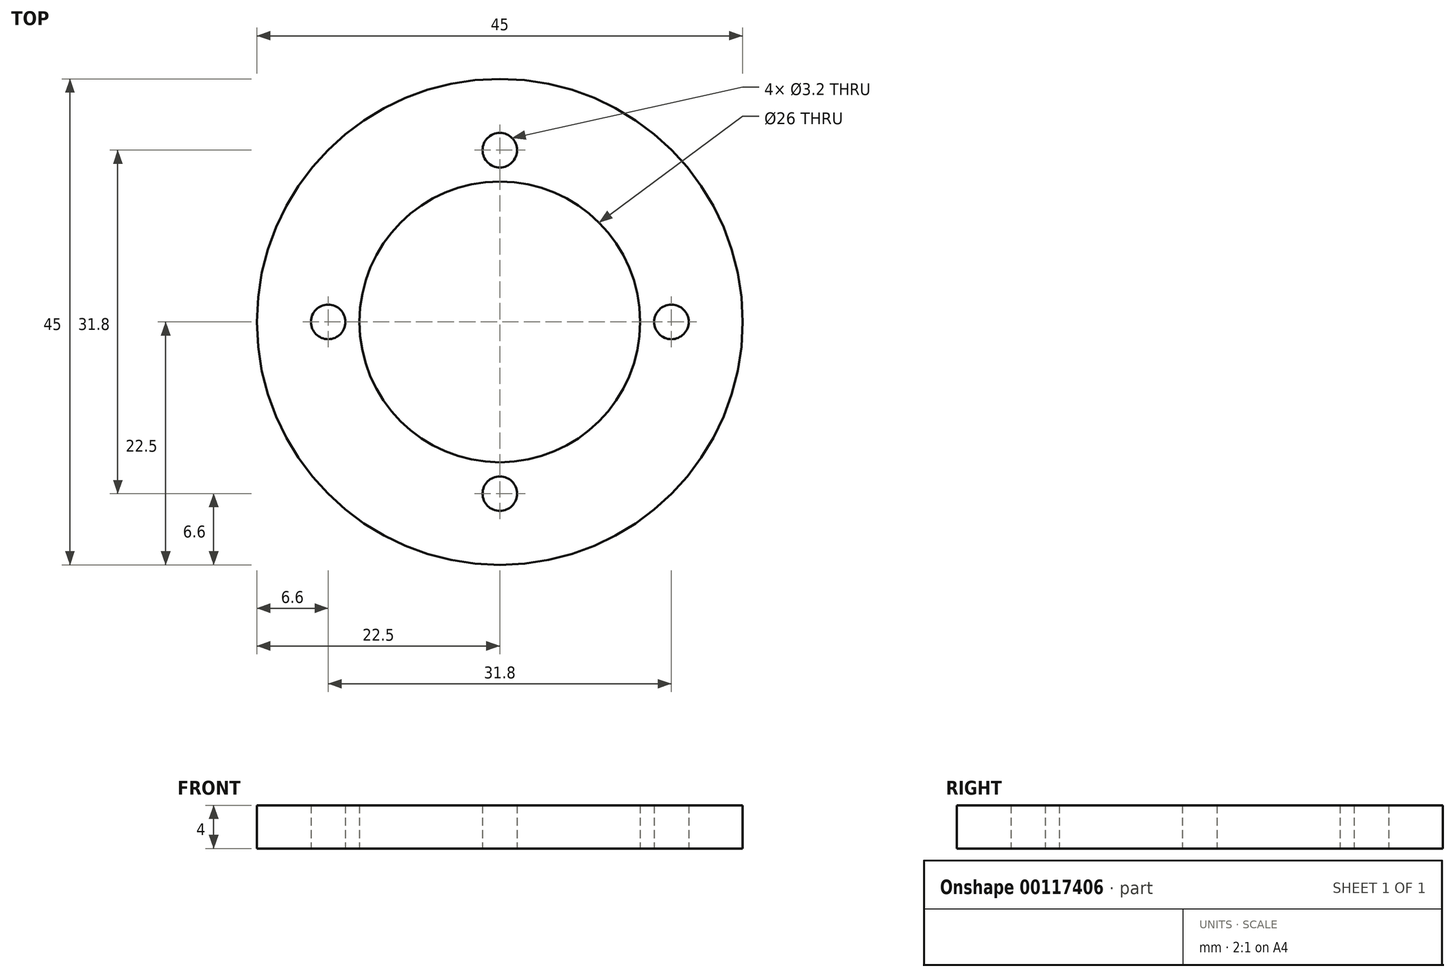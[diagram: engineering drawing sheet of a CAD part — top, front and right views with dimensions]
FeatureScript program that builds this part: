
annotation { "Feature Type Name" : "Feature", "Feature Type Description" : "" }
export const myFeature = defineFeature(function(context is Context, id is Id, definition is map)
    precondition{}
    {
        {
            var Q0;
            Q0=qCreatedBy(makeId("Top.planeOp"),FACE);
            var sketch = newSketch(context, id + "F0", { "sketchPlane" : qUnion([Q0])});
            skCircle(sketch, "E0", {"center": v(0, 0) * mm, "radius": 22.5 * mm});
            skCircle(sketch, "E1", {"center": v(0, 15.9) * mm, "radius": 1.6 * mm});
            skCircle(sketch, "E2.1.0", {"center": v(15.9, 0) * mm, "radius": 1.6 * mm});
            skCircle(sketch, "E2.2.0", {"center": v(0, -15.9) * mm, "radius": 1.6 * mm});
            skCircle(sketch, "E2.3.0", {"center": v(-15.9, 0) * mm, "radius": 1.6 * mm});
            skLineSegment(sketch, "E2.anchor1", {"start": v(0, 0) * mm, "end": v(0, 15.9) * mm, "construction": true});
            skLineSegment(sketch, "E2.anchor2", {"start": v(0, 0) * mm, "end": v(-15.9, 0) * mm, "construction": true});
            skLineSegment(sketch, "E3", {"start": v(-10.17, 17.5) * mm, "end": v(10.6, 17.5) * mm, "construction": true});
            skLineSegment(sketch, "E4", {"start": v(10.6, -17.5) * mm, "end": v(-12.33, -17.5) * mm, "construction": true});
            skCircle(sketch, "E5", {"center": v(0, 0) * mm, "radius": 13 * mm});
            skSolve(sketch);
        }
        {
            var Q0;
            Q0 = qSketchRegion(id + "F0", true);
            extrude(context, id + "F1", {"entities" : qUnion([Q0]), "depth" : 4 * mm});
        }
    });
